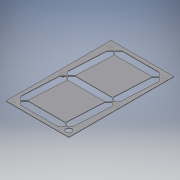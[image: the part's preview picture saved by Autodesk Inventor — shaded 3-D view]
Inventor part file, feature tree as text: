
AUTODESK INVENTOR PART (.ipt)
format: ipt  version: 2016 SP2 (Build 200236200, 236)  size: 184,832 bytes
history: native  units: mm
features: reference x5, extrude x2, sketch x2
ambient origin geometry x8: Origin, YZ Plane, XZ Plane, XY Plane, X Axis, Y Axis, Z Axis, Center Point
bodies: Volumenkörper1 (feature_tree)
feature tree (9):
  extrude  "Extrusion1"  Depth=8.0mm
  extrude  "Extrusion2"  Depth=5.0mm
  sketch  "Skizze1"  dims[d24=8.0mm d25=8.0mm]
  sketch  "Skizze3"  dims[d26=8.0mm d27=5.0mm d28=10.0mm d30=1.0mm d31=0.523599mm d32=0.0mm d33=10.0mm d34=135.0deg d35=1.0mm d36=0.0mm d37=1.0mm d38=0.0mm d39=1.0mm d40=0.0mm d41=1.0mm d42=5.0mm d43=10.0mm d44=1.0mm d45=1.0mm d46=0.6mm d47=0.0mm d48=50.0mm d49=85.233596mm d50=142.691381mm d51=4.8mm d52=4.8mm d53=4.8mm d54=4.8mm d55=4.8mm d56=2.5mm d57=0.0mm]
  reference  "Referenz1"
  reference  "Referenz2"
  reference  "Referenz3"
  reference  "Referenz4"
  reference  "Referenz5"
